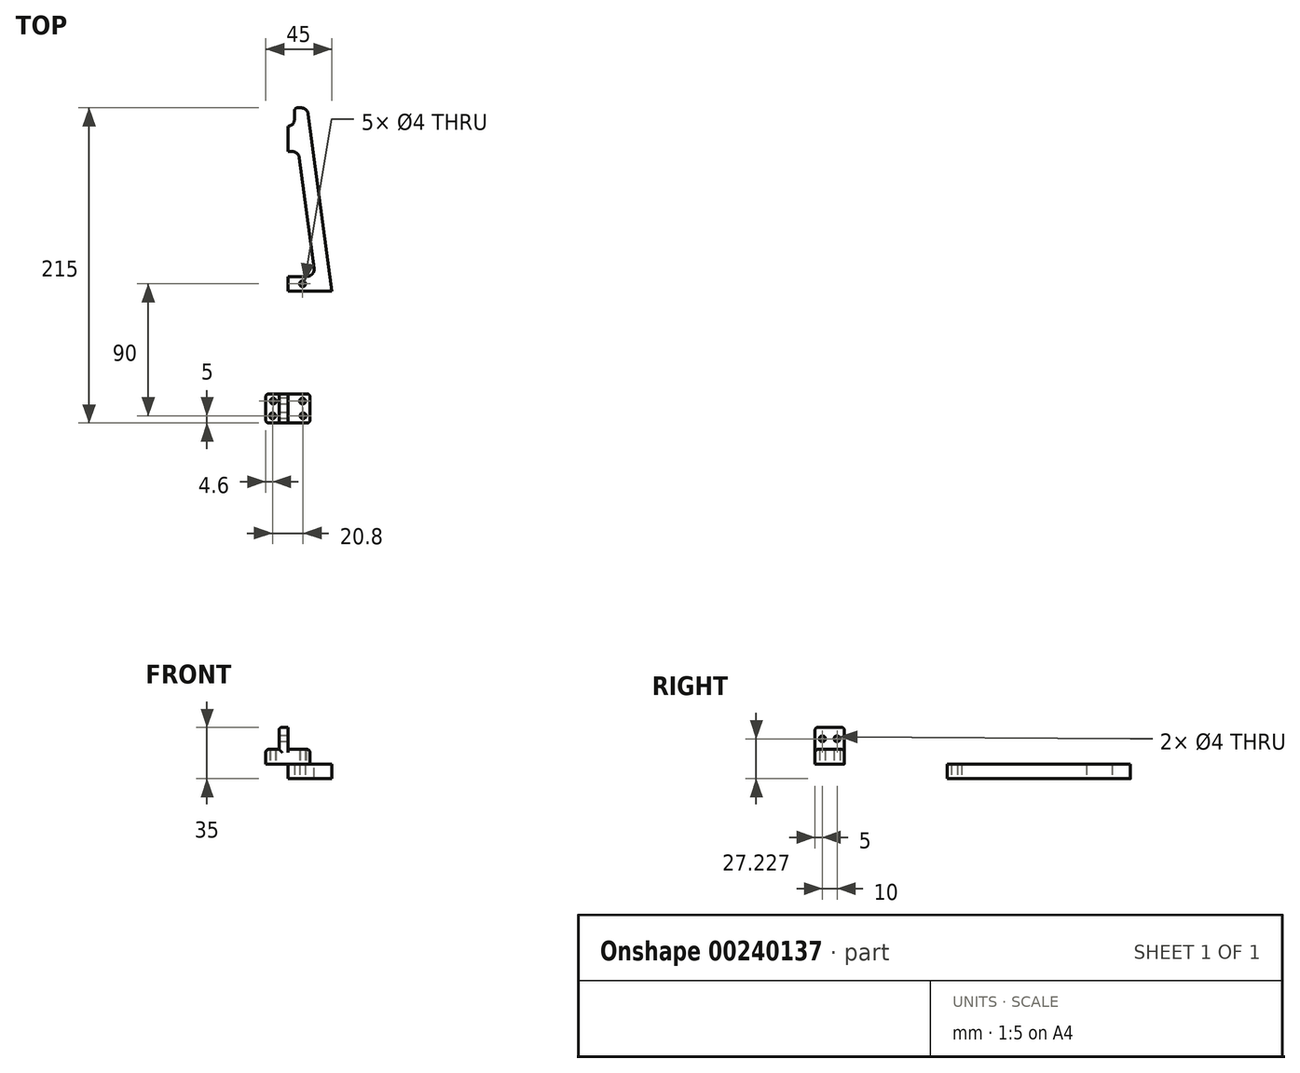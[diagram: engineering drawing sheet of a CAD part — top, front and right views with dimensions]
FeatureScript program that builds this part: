
annotation { "Feature Type Name" : "Feature", "Feature Type Description" : "" }
export const myFeature = defineFeature(function(context is Context, id is Id, definition is map)
    precondition{}
    {
        {
            var Q0;
            Q0=qCreatedBy(makeId("Top.planeOp"),FACE);
            var sketch = newSketch(context, id + "F0", { "sketchPlane" : qUnion([Q0])});
            skLineSegment(sketch, "E0.top", {"start": v(0, 75) * mm, "end": v(-30, 75) * mm});
            skPoint(sketch, "E0.middle", {"position": v(0, 0) * mm});
            skLineSegment(sketch, "E1", {"start": v(-30, 75) * mm, "end": v(-50, -75) * mm});
            skPoint(sketch, "E0.right.end.orphan", {"position": v(-50, 75) * mm});
            skPoint(sketch, "E0.left.end.orphan", {"position": v(50, 75) * mm});
            skLineSegment(sketch, "E2", {"start": v(0, 0) * mm, "end": v(0, 6) * mm});
            skLineSegment(sketch, "E3", {"start": v(-50, -75) * mm, "end": v(-40, -75) * mm});
            skLineSegment(sketch, "E4", {"start": v(-30, 75) * mm, "end": v(-20, 75) * mm});
            skLineSegment(sketch, "E5", {"start": v(0, 75) * mm, "end": v(0, 65) * mm});
            skLineSegment(sketch, "E6", {"start": v(0, 65) * mm, "end": v(-21.33, 65) * mm});
            skLineSegment(sketch, "E7", {"start": v(0, -75) * mm, "end": v(0, -65) * mm});
            skLineSegment(sketch, "E8", {"start": v(0, -65) * mm, "end": v(-38.67, -65) * mm});
            skLineSegment(sketch, "E9", {"start": v(0, 6) * mm, "end": v(-29.2, 6) * mm});
            skLineSegment(sketch, "E10", {"start": v(0, 0) * mm, "end": v(0, -6) * mm});
            skLineSegment(sketch, "E11", {"start": v(0, -6) * mm, "end": v(-30.8, -6) * mm});
            skLineSegment(sketch, "E12.trimOffspring", {"start": v(-30.8, -6) * mm, "end": v(-38.67, -65) * mm});
            skLineSegment(sketch, "E13", {"start": v(-21.33, 65) * mm, "end": v(-29.2, 6) * mm});
            skLineSegment(sketch, "E14.trimOffspring", {"start": v(0, -75) * mm, "end": v(-50, -75) * mm});
            skPoint(sketch, "E0.bottom.start.orphan", {"position": v(50, -75) * mm});
            skCircle(sketch, "E15", {"center": v(-15, 0) * mm, "radius": 2 * mm});
            skLineSegment(sketch, "E16", {"start": v(0, 65) * mm, "end": v(0, 70) * mm});
            skCircle(sketch, "E17", {"center": v(-10.41, 70) * mm, "radius": 2 * mm});
            skSolve(sketch);
        }
        {
            var Q0;
            Q0=qSketchRegion(id+"F0",true);
            extrude(context, id + "F1", {"entities" : qUnion([Q0]), "depth" : 10 * mm});
        }
        {
            var Q0;
            Q0=makeQuery(id+"F1.opExtrude","SWEPT_EDGE",EDGE,{"disambiguationData":[OSD([sQuery(id+"F0.wireOp",EDGE,"E6"),sQuery(id+"F0.wireOp",EDGE,"E13")])]});
            var Q1;
            Q1=makeQuery(id+"F1.opExtrude","SWEPT_EDGE",EDGE,{"disambiguationData":[OSD([sQuery(id+"F0.wireOp",EDGE,"E11"),sQuery(id+"F0.wireOp",EDGE,"E12.trimOffspring")])]});
            var Q2;
            Q2=makeQuery(id+"F1.opExtrude","SWEPT_EDGE",EDGE,{"disambiguationData":[OSD([sQuery(id+"F0.wireOp",EDGE,"E9"),sQuery(id+"F0.wireOp",EDGE,"E13")])]});
            var Q3;
            Q3=makeQuery(id+"F1.opExtrude","SWEPT_EDGE",EDGE,{"disambiguationData":[OSD([sQuery(id+"F0.wireOp",EDGE,"E8"),sQuery(id+"F0.wireOp",EDGE,"E12.trimOffspring")])]});
            var Q4;
            Q4=makeQuery(id+"F1.opExtrude","SWEPT_EDGE",EDGE,{"disambiguationData":[OSD([sQuery(id+"F0.wireOp",EDGE,"E1"),sQuery(id+"F0.wireOp",EDGE,"E14.trimOffspring")])]});
            fillet(context, id + "F2", {"entities" : qUnion([Q0, Q1, Q2, Q3, Q4]), "radius" : 5 * mm, "tangentPropagation" : true, "allowEdgeOverflow" : false});
        }
        {
            var Q0;
            Q0=makeQuery(id+"F1.opExtrude","SWEPT_BODY",BODY,{"disambiguationData":[OSD([sQuery(id+"F0.wireOp",EDGE,"E0.top"),sQuery(id+"F0.wireOp",EDGE,"E1"),sQuery(id+"F0.wireOp",EDGE,"E2"),sQuery(id+"F0.wireOp",EDGE,"E4"),sQuery(id+"F0.wireOp",EDGE,"E5"),sQuery(id+"F0.wireOp",EDGE,"E6"),sQuery(id+"F0.wireOp",EDGE,"E7"),sQuery(id+"F0.wireOp",EDGE,"E8"),sQuery(id+"F0.wireOp",EDGE,"E9"),sQuery(id+"F0.wireOp",EDGE,"E10"),sQuery(id+"F0.wireOp",EDGE,"E11"),sQuery(id+"F0.wireOp",EDGE,"E12.trimOffspring"),sQuery(id+"F0.wireOp",EDGE,"E13"),sQuery(id+"F0.wireOp",EDGE,"E14.trimOffspring"),sQuery(id+"F0.wireOp",EDGE,"E15"),sQuery(id+"F0.wireOp",EDGE,"E16"),sQuery(id+"F0.wireOp",EDGE,"E17")])]});
            var Q1;
            Q1=qCreatedBy(makeId("Right.planeOp"),FACE);
            mirror(context, id + "F3", {"operationType" : NewBodyOperationType.ADD, "entities" : qUnion([Q0]), "mirrorPlane" : qUnion([Q1])});
        }
        {
            var Q0;
            Q0=qCreatedBy(makeId("Top.planeOp"),FACE);
            var sketch = newSketch(context, id + "F4", { "sketchPlane" : qUnion([Q0])});
            skLineSegment(sketch, "E18", {"start": v(0, 0) * mm, "end": v(40, 0) * mm});
            skLineSegment(sketch, "E19", {"start": v(0, 75) * mm, "end": v(30, 75) * mm});
            skLineSegment(sketch, "E20", {"start": v(0, 75) * mm, "end": v(0, 85) * mm});
            skLineSegment(sketch, "E21", {"start": v(4.5, 200) * mm, "end": v(13.33, 200) * mm});
            skLineSegment(sketch, "E22", {"start": v(30, 75) * mm, "end": v(13.33, 200) * mm});
            skArc(sketch, "E23", {"start": v(0, 187.5) * mm, "mid": v(3.18, 188.82) * mm, "end": v(4.5, 192) * mm});
            skLineSegment(sketch, "E24", {"start": v(4.5, 200) * mm, "end": v(4.5, 192) * mm});
            skLineSegment(sketch, "E25", {"start": v(0, 75) * mm, "end": v(0, 80) * mm});
            skCircle(sketch, "E26", {"center": v(10, 80) * mm, "radius": 2 * mm});
            skLineSegment(sketch, "E27", {"start": v(0, 75) * mm, "end": v(10, 75) * mm});
            skLineSegment(sketch, "E28", {"start": v(10, 85) * mm, "end": v(18.67, 85) * mm});
            skLineSegment(sketch, "E29", {"start": v(18.67, 85) * mm, "end": v(10, 150) * mm});
            skLineSegment(sketch, "E30", {"start": v(10, 85) * mm, "end": v(0, 85) * mm});
            skLineSegment(sketch, "E31", {"start": v(18.67, 85) * mm, "end": v(7.31, 170.17) * mm});
            skLineSegment(sketch, "E32", {"start": v(7.31, 170.17) * mm, "end": v(0, 170.17) * mm});
            skLineSegment(sketch, "E33.trimOffspring", {"start": v(0, 170.17) * mm, "end": v(0, 187.5) * mm});
            skSolve(sketch);
        }
        {
            var Q0;
            Q0=qSketchRegion(id+"F4",true);
            extrude(context, id + "F5", {"entities" : qUnion([Q0]), "depth" : 10 * mm});
        }
        {
            var Q0;
            Q0=makeQuery(id+"F5.opExtrude","SWEPT_BODY",BODY,{"disambiguationData":[OSD([sQuery(id+"F4.wireOp",EDGE,"E19"),sQuery(id+"F4.wireOp",EDGE,"E20"),sQuery(id+"F4.wireOp",EDGE,"E21"),sQuery(id+"F4.wireOp",EDGE,"E22"),sQuery(id+"F4.wireOp",EDGE,"E23"),sQuery(id+"F4.wireOp",EDGE,"E24"),sQuery(id+"F4.wireOp",EDGE,"E25"),sQuery(id+"F4.wireOp",EDGE,"E26"),sQuery(id+"F4.wireOp",EDGE,"E27"),sQuery(id+"F4.wireOp",EDGE,"E28"),sQuery(id+"F4.wireOp",EDGE,"E30"),sQuery(id+"F4.wireOp",EDGE,"E31"),sQuery(id+"F4.wireOp",EDGE,"E32"),sQuery(id+"F4.wireOp",EDGE,"E33.trimOffspring")])]});
            var Q1;
            Q1=qCreatedBy(makeId("Right.planeOp"),FACE);
            mirror(context, id + "F6", {"entities" : qUnion([Q0]), "mirrorPlane" : qUnion([Q1])});
        }
        {
            var Q0;
            Q0=makeQuery(id+"F6.opPattern","COPY",EDGE,{"derivedFrom":makeQuery(id+"F5.opExtrude","SWEPT_EDGE",EDGE,{"disambiguationData":[OSD([sQuery(id+"F4.wireOp",EDGE,"E31"),sQuery(id+"F4.wireOp",EDGE,"E32")])]}),"instanceName":"1"});
            var Q1;
            Q1=makeQuery(id+"F5.opExtrude","SWEPT_EDGE",EDGE,{"disambiguationData":[OSD([sQuery(id+"F4.wireOp",EDGE,"E31"),sQuery(id+"F4.wireOp",EDGE,"E32")])]});
            var Q2;
            Q2=makeQuery(id+"F6.opPattern","COPY",EDGE,{"derivedFrom":makeQuery(id+"F5.opExtrude","SWEPT_EDGE",EDGE,{"disambiguationData":[OSD([sQuery(id+"F4.wireOp",EDGE,"E28"),sQuery(id+"F4.wireOp",EDGE,"E31")])]}),"instanceName":"1"});
            var Q3;
            Q3=makeQuery(id+"F5.opExtrude","SWEPT_EDGE",EDGE,{"disambiguationData":[OSD([sQuery(id+"F4.wireOp",EDGE,"E28"),sQuery(id+"F4.wireOp",EDGE,"E31")])]});
            var Q4;
            Q4=makeQuery(id+"F6.opPattern","COPY",EDGE,{"derivedFrom":makeQuery(id+"F5.opExtrude","SWEPT_EDGE",EDGE,{"disambiguationData":[OSD([sQuery(id+"F4.wireOp",EDGE,"E21"),sQuery(id+"F4.wireOp",EDGE,"E22")])]}),"instanceName":"1"});
            var Q5;
            Q5=makeQuery(id+"F5.opExtrude","SWEPT_EDGE",EDGE,{"disambiguationData":[OSD([sQuery(id+"F4.wireOp",EDGE,"E21"),sQuery(id+"F4.wireOp",EDGE,"E22")])]});
            fillet(context, id + "F7", {"entities" : qUnion([Q0, Q1, Q2, Q3, Q4, Q5]), "radius" : 5 * mm, "tangentPropagation" : true, "allowEdgeOverflow" : false});
        }
        {
            var Q0;
            Q0=makeQuery(id+"F5.opExtrude","SWEPT_EDGE",EDGE,{"disambiguationData":[OSD([sQuery(id+"F4.wireOp",EDGE,"E21"),sQuery(id+"F4.wireOp",EDGE,"E24")])]});
            var Q1;
            Q1=makeQuery(id+"F6.opPattern","COPY",EDGE,{"derivedFrom":makeQuery(id+"F5.opExtrude","SWEPT_EDGE",EDGE,{"disambiguationData":[OSD([sQuery(id+"F4.wireOp",EDGE,"E21"),sQuery(id+"F4.wireOp",EDGE,"E24")])]}),"instanceName":"1"});
            fillet(context, id + "F8", {"entities" : qUnion([Q0, Q1]), "radius" : 2 * mm, "tangentPropagation" : true, "allowEdgeOverflow" : false});
        }
        {
            var Q0;
            Q0=qCreatedBy(makeId("Top.planeOp"),FACE);
            var sketch = newSketch(context, id + "F9", { "sketchPlane" : qUnion([Q0])});
            skLineSegment(sketch, "E34", {"start": v(0, 0) * mm, "end": v(0, 6) * mm});
            skLineSegment(sketch, "E35", {"start": v(0, 6) * mm, "end": v(-6, 6) * mm});
            skLineSegment(sketch, "E36", {"start": v(-6, 6) * mm, "end": v(-6, -6) * mm});
            skLineSegment(sketch, "E37", {"start": v(-6, -6) * mm, "end": v(0, -6) * mm});
            skLineSegment(sketch, "E38", {"start": v(0, -6) * mm, "end": v(0, 0) * mm});
            skSolve(sketch);
        }
        {
            var Q0;
            Q0=qSketchRegion(id+"F9",true);
            extrude(context, id + "F10", {"entities" : qUnion([Q0]), "operationType" : NewBodyOperationType.ADD, "depth" : 25 * mm});
        }
        {
            var Q0;
            Q0=makeQuery(id+"F10.opExtrude","SWEPT_EDGE",EDGE,{"disambiguationData":[OSD([sQuery(id+"F9.wireOp",EDGE,"E36"),sQuery(id+"F9.wireOp",EDGE,"E37")])]});
            var Q1;
            Q1=makeQuery(id+"F10.opExtrude","CAP_EDGE",EDGE,{"disambiguationData":[OSD([sQuery(id+"F9.wireOp",EDGE,"E36")])],"isStart":false});
            var Q2;
            Q2=makeQuery(id+"F10.opExtrude","CAP_EDGE",EDGE,{"disambiguationData":[OSD([sQuery(id+"F9.wireOp",EDGE,"E37")])],"isStart":false});
            var Q3;
            Q3=makeQuery(id+"F10.opExtrude","SWEPT_EDGE",EDGE,{"disambiguationData":[OSD([sQuery(id+"F9.wireOp",EDGE,"E35"),sQuery(id+"F9.wireOp",EDGE,"E36")])]});
            var Q4;
            Q4=makeQuery(id+"F10.opExtrude","CAP_EDGE",EDGE,{"disambiguationData":[OSD([sQuery(id+"F9.wireOp",EDGE,"E35")])],"isStart":false});
            fillet(context, id + "F11", {"entities" : qUnion([Q0, Q1, Q2, Q3, Q4]), "radius" : 1.5 * mm, "tangentPropagation" : true, "allowEdgeOverflow" : false});
        }
        {
            var Q0;
            Q0=qCreatedBy(makeId("Right.planeOp"),FACE);
            var sketch = newSketch(context, id + "F12", { "sketchPlane" : qUnion([Q0])});
            skCircle(sketch, "E39", {"center": v(0, 20) * mm, "radius": 1.75 * mm});
            skCircle(sketch, "E40", {"center": v(0, 15) * mm, "radius": 1.75 * mm});
            skSolve(sketch);
        }
        {
            var Q0;
            Q0=qSketchRegion(id+"F12",true);
            extrude(context, id + "F13", {"entities" : qUnion([Q0]), "endBound" : BoundingType.SYMMETRIC, "depth" : 25 * mm});
        }
        {
            var Q0;
            Q0=makeQuery(id+"F13.opExtrude","SWEPT_BODY",BODY,{"disambiguationData":[OSD([sQuery(id+"F12.wireOp",EDGE,"E40")])]});
            var Q1;
            Q1=makeQuery(id+"F13.opExtrude","SWEPT_BODY",BODY,{"disambiguationData":[OSD([sQuery(id+"F12.wireOp",EDGE,"E39")])]});
            var Q2;
            Q2=makeQuery(id+"F1.opExtrude","SWEPT_BODY",BODY,{"disambiguationData":[OSD([sQuery(id+"F0.wireOp",EDGE,"E0.top"),sQuery(id+"F0.wireOp",EDGE,"E1"),sQuery(id+"F0.wireOp",EDGE,"E2"),sQuery(id+"F0.wireOp",EDGE,"E4"),sQuery(id+"F0.wireOp",EDGE,"E5"),sQuery(id+"F0.wireOp",EDGE,"E6"),sQuery(id+"F0.wireOp",EDGE,"E7"),sQuery(id+"F0.wireOp",EDGE,"E8"),sQuery(id+"F0.wireOp",EDGE,"E9"),sQuery(id+"F0.wireOp",EDGE,"E10"),sQuery(id+"F0.wireOp",EDGE,"E11"),sQuery(id+"F0.wireOp",EDGE,"E12.trimOffspring"),sQuery(id+"F0.wireOp",EDGE,"E13"),sQuery(id+"F0.wireOp",EDGE,"E14.trimOffspring"),sQuery(id+"F0.wireOp",EDGE,"E15"),sQuery(id+"F0.wireOp",EDGE,"E16"),sQuery(id+"F0.wireOp",EDGE,"E17")])]});
            booleanBodies(context, id + "F14", {"operationType" : BooleanOperationType.SUBTRACTION, "tools" : qUnion([Q0, Q1]), "targets" : qUnion([Q2])});
        }
        {
            var Q0;
            Q0=qCreatedBy(makeId("Top.planeOp"),FACE);
            var sketch = newSketch(context, id + "F15", { "sketchPlane" : qUnion([Q0])});
            skLineSegment(sketch, "E41.bottom", {"start": v(15, 65) * mm, "end": v(-15, 65) * mm});
            skLineSegment(sketch, "E41.top", {"start": v(15, 85) * mm, "end": v(-15, 85) * mm});
            skLineSegment(sketch, "E41.left", {"start": v(15, 65) * mm, "end": v(15, 85) * mm});
            skLineSegment(sketch, "E41.right", {"start": v(-15, 65) * mm, "end": v(-15, 85) * mm});
            skPoint(sketch, "E41.middle", {"position": v(0, 75) * mm});
            skLineSegment(sketch, "E42", {"start": v(0, 75) * mm, "end": v(0, 85) * mm});
            skLineSegment(sketch, "E43", {"start": v(0, 85) * mm, "end": v(0, 65) * mm});
            skLineSegment(sketch, "E44", {"start": v(0, 65) * mm, "end": v(-6, 65) * mm});
            skLineSegment(sketch, "E45", {"start": v(-6, 65) * mm, "end": v(-6, 85) * mm});
            skLineSegment(sketch, "E46", {"start": v(-6, 85) * mm, "end": v(0, 85) * mm});
            skSolve(sketch);
        }
        {
            var Q0;
            Q0=qSketchRegion(id+"F15",true);
            extrude(context, id + "F16", {"entities" : qUnion([Q0]), "depth" : 10 * mm});
        }
        {
            var Q0;
            Q0=qCreatedBy(makeId("Top.planeOp"),FACE);
            var sketch = newSketch(context, id + "F17", { "sketchPlane" : qUnion([Q0])});
            skLineSegment(sketch, "E47", {"start": v(0, 65) * mm, "end": v(0, 85) * mm});
            skLineSegment(sketch, "E48", {"start": v(0, 85) * mm, "end": v(-6, 85) * mm});
            skLineSegment(sketch, "E49", {"start": v(-6, 85) * mm, "end": v(-6, 65) * mm});
            skLineSegment(sketch, "E50", {"start": v(-6, 65) * mm, "end": v(0, 65) * mm});
            skSolve(sketch);
        }
        {
            var Q0;
            Q0=qSketchRegion(id+"F17",true);
            extrude(context, id + "F18", {"entities" : qUnion([Q0]), "depth" : 25 * mm});
        }
        {
            var Q0;
            Q0=makeQuery(id+"F16.opExtrude","SWEPT_BODY",BODY,{"disambiguationData":[OSD([sQuery(id+"F15.wireOp",EDGE,"E41.bottom"),sQuery(id+"F15.wireOp",EDGE,"E41.top"),sQuery(id+"F15.wireOp",EDGE,"E41.left"),sQuery(id+"F15.wireOp",EDGE,"E41.right"),sQuery(id+"F15.wireOp",EDGE,"E44"),sQuery(id+"F15.wireOp",EDGE,"E46")])]});
            var Q1;
            Q1=makeQuery(id+"F18.opExtrude","SWEPT_BODY",BODY,{"disambiguationData":[OSD([sQuery(id+"F17.wireOp",EDGE,"E47"),sQuery(id+"F17.wireOp",EDGE,"E48"),sQuery(id+"F17.wireOp",EDGE,"E49"),sQuery(id+"F17.wireOp",EDGE,"E50")])]});
            booleanBodies(context, id + "F19", {"operationType" : BooleanOperationType.UNION, "tools" : qUnion([Q0, Q1])});
        }
        {
            var Q0;
            Q0=makeQuery(id+"F16.opExtrude","SWEPT_BODY",BODY,{"disambiguationData":[OSD([sQuery(id+"F15.wireOp",EDGE,"E41.bottom"),sQuery(id+"F15.wireOp",EDGE,"E41.top"),sQuery(id+"F15.wireOp",EDGE,"E41.left"),sQuery(id+"F15.wireOp",EDGE,"E41.right"),sQuery(id+"F15.wireOp",EDGE,"E44"),sQuery(id+"F15.wireOp",EDGE,"E46")])]});
            transform(context, id + "F20", {"entities" : qUnion([Q0]), "transformType" : TransformType.TRANSLATION_3D, "dx" : 0 * mm, "dy" : 0 * mm, "dz" : 10 * mm, "makeCopy" : false});
        }
        {
            var Q0;
            Q0=qCreatedBy(makeId("Top.planeOp"),FACE);
            var sketch = newSketch(context, id + "F21", { "sketchPlane" : qUnion([Q0])});
            skCircle(sketch, "E51", {"center": v(-10, 80) * mm, "radius": 2 * mm});
            skCircle(sketch, "E52", {"center": v(10, 80) * mm, "radius": 2 * mm});
            skCircle(sketch, "E53", {"center": v(-10.4, 70) * mm, "radius": 2 * mm});
            skCircle(sketch, "E54", {"center": v(10.4, 70) * mm, "radius": 2 * mm});
            skSolve(sketch);
        }
        {
            var Q0;
            Q0=qSketchRegion(id+"F21",true);
            extrude(context, id + "F22", {"entities" : qUnion([Q0]), "depth" : 30 * mm});
        }
        {
            var Q0;
            Q0=makeQuery(id+"F22.opExtrude","SWEPT_BODY",BODY,{"disambiguationData":[OSD([sQuery(id+"F21.wireOp",EDGE,"E54")])]});
            var Q1;
            Q1=makeQuery(id+"F22.opExtrude","SWEPT_BODY",BODY,{"disambiguationData":[OSD([sQuery(id+"F21.wireOp",EDGE,"E53")])]});
            var Q2;
            Q2=makeQuery(id+"F22.opExtrude","SWEPT_BODY",BODY,{"disambiguationData":[OSD([sQuery(id+"F21.wireOp",EDGE,"E52")])]});
            var Q3;
            Q3=makeQuery(id+"F22.opExtrude","SWEPT_BODY",BODY,{"disambiguationData":[OSD([sQuery(id+"F21.wireOp",EDGE,"E51")])]});
            var Q4;
            Q4=makeQuery(id+"F16.opExtrude","SWEPT_BODY",BODY,{"disambiguationData":[OSD([sQuery(id+"F15.wireOp",EDGE,"E41.bottom"),sQuery(id+"F15.wireOp",EDGE,"E41.top"),sQuery(id+"F15.wireOp",EDGE,"E41.left"),sQuery(id+"F15.wireOp",EDGE,"E41.right"),sQuery(id+"F15.wireOp",EDGE,"E44"),sQuery(id+"F15.wireOp",EDGE,"E46")])]});
            booleanBodies(context, id + "F23", {"operationType" : BooleanOperationType.SUBTRACTION, "tools" : qUnion([Q0, Q1, Q2, Q3]), "targets" : qUnion([Q4])});
        }
        {
            var Q0;
            Q0=qCreatedBy(makeId("Right.planeOp"),FACE);
            var sketch = newSketch(context, id + "F24", { "sketchPlane" : qUnion([Q0])});
            skCircle(sketch, "E55", {"center": v(80, 27.23) * mm, "radius": 2 * mm});
            skCircle(sketch, "E56", {"center": v(70, 27.23) * mm, "radius": 2 * mm});
            skSolve(sketch);
        }
        {
            var Q0;
            Q0=qSketchRegion(id+"F24",true);
            extrude(context, id + "F25", {"entities" : qUnion([Q0]), "endBound" : BoundingType.SYMMETRIC, "depth" : 25 * mm});
        }
        {
            var Q0;
            Q0=makeQuery(id+"F25.opExtrude","SWEPT_BODY",BODY,{"disambiguationData":[OSD([sQuery(id+"F24.wireOp",EDGE,"E56")])]});
            var Q1;
            Q1=makeQuery(id+"F25.opExtrude","SWEPT_BODY",BODY,{"disambiguationData":[OSD([sQuery(id+"F24.wireOp",EDGE,"E55")])]});
            var Q2;
            Q2=makeQuery(id+"F16.opExtrude","SWEPT_BODY",BODY,{"disambiguationData":[OSD([sQuery(id+"F15.wireOp",EDGE,"E41.bottom"),sQuery(id+"F15.wireOp",EDGE,"E41.top"),sQuery(id+"F15.wireOp",EDGE,"E41.left"),sQuery(id+"F15.wireOp",EDGE,"E41.right"),sQuery(id+"F15.wireOp",EDGE,"E44"),sQuery(id+"F15.wireOp",EDGE,"E46")])]});
            booleanBodies(context, id + "F26", {"operationType" : BooleanOperationType.SUBTRACTION, "tools" : qUnion([Q0, Q1]), "targets" : qUnion([Q2])});
        }
        {
            var Q0;
            Q0=makeQuery(id+"F18.opExtrude","SWEPT_EDGE",EDGE,{"disambiguationData":[OSD([sQuery(id+"F17.wireOp",EDGE,"E49"),sQuery(id+"F17.wireOp",EDGE,"E50")])]});
            var Q1;
            Q1=makeQuery(id+"F18.opExtrude","CAP_EDGE",EDGE,{"disambiguationData":[OSD([sQuery(id+"F17.wireOp",EDGE,"E50")])],"isStart":false});
            var Q2;
            {var subQ0=sQuery(id+"F15.wireOp",EDGE,"E44");var subQ1=sQuery(id+"F15.wireOp",EDGE,"E41.bottom");var subQ2=sQuery(id+"F15.wireOp",EDGE,"E41.right");Q2=makeQuery(id+"F19.opBoolean","SPLIT",EDGE,{"disambiguationData":[TD([makeQuery(id+"F16.opExtrude","SWEPT_FACE",FACE,{"disambiguationData":[OSD([subQ2])]})])],"derivedFrom":makeQuery(id+"F16.opExtrude","CAP_EDGE",EDGE,{"disambiguationData":[OSD([subQ1,subQ0])],"isStart":false})});}
            var Q3;
            Q3=makeQuery(id+"F16.opExtrude","SWEPT_EDGE",EDGE,{"disambiguationData":[OSD([sQuery(id+"F15.wireOp",EDGE,"E41.bottom"),sQuery(id+"F15.wireOp",EDGE,"E41.right")])]});
            var Q4;
            {var subQ0=sQuery(id+"F15.wireOp",EDGE,"E41.left");var subQ1=sQuery(id+"F15.wireOp",EDGE,"E44");var subQ2=sQuery(id+"F15.wireOp",EDGE,"E41.bottom");Q4=makeQuery(id+"F19.opBoolean","SPLIT",EDGE,{"disambiguationData":[TD([makeQuery(id+"F16.opExtrude","SWEPT_FACE",FACE,{"disambiguationData":[OSD([subQ0])]})])],"derivedFrom":makeQuery(id+"F16.opExtrude","CAP_EDGE",EDGE,{"disambiguationData":[OSD([subQ2,subQ1])],"isStart":false})});}
            var Q5;
            Q5=makeQuery(id+"F16.opExtrude","SWEPT_EDGE",EDGE,{"disambiguationData":[OSD([sQuery(id+"F15.wireOp",EDGE,"E41.bottom"),sQuery(id+"F15.wireOp",EDGE,"E41.left")])]});
            var Q6;
            Q6=makeQuery(id+"F16.opExtrude","CAP_EDGE",EDGE,{"disambiguationData":[OSD([sQuery(id+"F15.wireOp",EDGE,"E41.left")])],"isStart":false});
            var Q7;
            Q7=makeQuery(id+"F16.opExtrude","CAP_EDGE",EDGE,{"disambiguationData":[OSD([sQuery(id+"F15.wireOp",EDGE,"E41.right")])],"isStart":false});
            var Q8;
            Q8=makeQuery(id+"F18.opExtrude","CAP_EDGE",EDGE,{"disambiguationData":[OSD([sQuery(id+"F17.wireOp",EDGE,"E49")])],"isStart":false});
            var Q9;
            {var subQ0=sQuery(id+"F15.wireOp",EDGE,"E41.right");var subQ1=sQuery(id+"F15.wireOp",EDGE,"E46");var subQ2=sQuery(id+"F15.wireOp",EDGE,"E41.top");Q9=makeQuery(id+"F19.opBoolean","SPLIT",EDGE,{"disambiguationData":[TD([makeQuery(id+"F16.opExtrude","SWEPT_FACE",FACE,{"disambiguationData":[OSD([subQ0])]})])],"derivedFrom":makeQuery(id+"F16.opExtrude","CAP_EDGE",EDGE,{"disambiguationData":[OSD([subQ2,subQ1])],"isStart":false})});}
            var Q10;
            Q10=makeQuery(id+"F16.opExtrude","SWEPT_EDGE",EDGE,{"disambiguationData":[OSD([sQuery(id+"F15.wireOp",EDGE,"E41.top"),sQuery(id+"F15.wireOp",EDGE,"E41.right")])]});
            var Q11;
            Q11=makeQuery(id+"F18.opExtrude","SWEPT_EDGE",EDGE,{"disambiguationData":[OSD([sQuery(id+"F17.wireOp",EDGE,"E48"),sQuery(id+"F17.wireOp",EDGE,"E49")])]});
            var Q12;
            Q12=makeQuery(id+"F18.opExtrude","CAP_EDGE",EDGE,{"disambiguationData":[OSD([sQuery(id+"F17.wireOp",EDGE,"E48")])],"isStart":false});
            var Q13;
            {var subQ0=sQuery(id+"F15.wireOp",EDGE,"E41.left");var subQ1=sQuery(id+"F15.wireOp",EDGE,"E46");var subQ2=sQuery(id+"F15.wireOp",EDGE,"E41.top");Q13=makeQuery(id+"F19.opBoolean","SPLIT",EDGE,{"disambiguationData":[TD([makeQuery(id+"F16.opExtrude","SWEPT_FACE",FACE,{"disambiguationData":[OSD([subQ0])]})])],"derivedFrom":makeQuery(id+"F16.opExtrude","CAP_EDGE",EDGE,{"disambiguationData":[OSD([subQ2,subQ1])],"isStart":false})});}
            var Q14;
            Q14=makeQuery(id+"F16.opExtrude","SWEPT_EDGE",EDGE,{"disambiguationData":[OSD([sQuery(id+"F15.wireOp",EDGE,"E41.top"),sQuery(id+"F15.wireOp",EDGE,"E41.left")])]});
            fillet(context, id + "F27", {"entities" : qUnion([Q0, Q1, Q2, Q3, Q4, Q5, Q6, Q7, Q8, Q9, Q10, Q11, Q12, Q13, Q14]), "radius" : 2 * mm, "tangentPropagation" : true, "allowEdgeOverflow" : false});
        }
        {
            var Q0;
            Q0=qCreatedBy(makeId("Right.planeOp"),FACE);
            var sketch = newSketch(context, id + "F28", { "sketchPlane" : qUnion([Q0])});
            skLineSegment(sketch, "E57", {"start": v(0, 0) * mm, "end": v(0, 10) * mm});
            skLineSegment(sketch, "E58", {"start": v(0, 10) * mm, "end": v(6, 10) * mm});
            skLineSegment(sketch, "E59", {"start": v(6, 10) * mm, "end": v(6, 25) * mm});
            skLineSegment(sketch, "E60", {"start": v(-6, 25) * mm, "end": v(-6, 10) * mm});
            skLineSegment(sketch, "E61", {"start": v(-6, 10) * mm, "end": v(0, 10) * mm});
            skLineSegment(sketch, "E62", {"start": v(75, 10) * mm, "end": v(75, 20) * mm});
            skLineSegment(sketch, "E63", {"start": v(75, 20) * mm, "end": v(85, 20) * mm});
            skLineSegment(sketch, "E64", {"start": v(85, 20) * mm, "end": v(85, 35) * mm});
            skLineSegment(sketch, "E65", {"start": v(65, 35) * mm, "end": v(65, 20) * mm});
            skLineSegment(sketch, "E66", {"start": v(65, 20) * mm, "end": v(75, 20) * mm});
            skLineSegment(sketch, "E67", {"start": v(-6, 10) * mm, "end": v(-6, 25) * mm});
            skLineSegment(sketch, "E68", {"start": v(75, 120) * mm, "end": v(85, 120) * mm});
            skLineSegment(sketch, "E69", {"start": v(85, 35) * mm, "end": v(85, 120) * mm});
            skLineSegment(sketch, "E70", {"start": v(85, 120) * mm, "end": v(75, 120) * mm});
            skLineSegment(sketch, "E71", {"start": v(6, 25) * mm, "end": v(65, 35) * mm});
            skLineSegment(sketch, "E72", {"start": v(-6, 25) * mm, "end": v(75, 120) * mm});
            skLineSegment(sketch, "E73", {"start": v(23.92, 44.68) * mm, "end": v(75, 104.59) * mm});
            skLineSegment(sketch, "E74", {"start": v(23.92, 44.68) * mm, "end": v(17.44, 37.08) * mm});
            skLineSegment(sketch, "E75", {"start": v(75, 45) * mm, "end": v(64.16, 45) * mm});
            skLineSegment(sketch, "E76", {"start": v(51.92, 42.93) * mm, "end": v(17.44, 37.08) * mm});
            skLineSegment(sketch, "E77", {"start": v(51.92, 42.93) * mm, "end": v(64.16, 45) * mm});
            skPoint(sketch, "E78.orphan", {"position": v(75, 35) * mm});
            skPoint(sketch, "E79.start.orphan", {"position": v(75, 110) * mm});
            skLineSegment(sketch, "E80", {"start": v(75, 104.59) * mm, "end": v(75, 45) * mm});
            skCircle(sketch, "E81", {"center": v(80, 110) * mm, "radius": 2 * mm});
            skCircle(sketch, "E82", {"center": v(80, 95) * mm, "radius": 2 * mm});
            skPoint(sketch, "E83.end.orphan", {"position": v(80, 120) * mm});
            skSolve(sketch);
        }
        {
            var Q0;
            Q0=qSketchRegion(id+"F28",true);
            extrude(context, id + "F29", {"entities" : qUnion([Q0]), "depth" : 8 * mm});
        }
        {
            var Q0;
            Q0=makeQuery(id+"F29.opExtrude","SWEPT_EDGE",EDGE,{"disambiguationData":[OSD([sQuery(id+"F28.wireOp",EDGE,"E73"),sQuery(id+"F28.wireOp",EDGE,"E80")])]});
            var Q1;
            Q1=makeQuery(id+"F29.opExtrude","SWEPT_EDGE",EDGE,{"disambiguationData":[OSD([sQuery(id+"F28.wireOp",EDGE,"E75"),sQuery(id+"F28.wireOp",EDGE,"E80")])]});
            var Q2;
            Q2=makeQuery(id+"F29.opExtrude","SWEPT_EDGE",EDGE,{"disambiguationData":[OSD([sQuery(id+"F28.wireOp",EDGE,"E74"),sQuery(id+"F28.wireOp",EDGE,"E76")])]});
            var Q3;
            Q3=makeQuery(id+"F29.opExtrude","SWEPT_EDGE",EDGE,{"disambiguationData":[OSD([sQuery(id+"F28.wireOp",EDGE,"E65"),sQuery(id+"F28.wireOp",EDGE,"E71")])]});
            var Q4;
            Q4=makeQuery(id+"F29.opExtrude","SWEPT_EDGE",EDGE,{"disambiguationData":[OSD([sQuery(id+"F28.wireOp",EDGE,"E59"),sQuery(id+"F28.wireOp",EDGE,"E71")])]});
            var Q5;
            Q5=makeQuery(id+"F29.opExtrude","SWEPT_EDGE",EDGE,{"disambiguationData":[OSD([sQuery(id+"F28.wireOp",EDGE,"E67"),sQuery(id+"F28.wireOp",EDGE,"E72")])]});
            fillet(context, id + "F30", {"entities" : qUnion([Q0, Q1, Q2, Q3, Q4, Q5]), "radius" : 2 * mm, "tangentPropagation" : true, "allowEdgeOverflow" : false});
        }
        {
            var Q0;
            Q0=makeQuery(id+"F29.opExtrude","CAP_EDGE",EDGE,{"disambiguationData":[OSD([sQuery(id+"F28.wireOp",EDGE,"E73"),sQuery(id+"F28.wireOp",EDGE,"E74")])],"isStart":false});
            var Q1;
            Q1=makeQuery(id+"F29.opExtrude","CAP_EDGE",EDGE,{"disambiguationData":[OSD([sQuery(id+"F28.wireOp",EDGE,"E72")])],"isStart":false});
            var Q2;
            Q2=makeQuery(id+"F29.opExtrude","CAP_EDGE",EDGE,{"disambiguationData":[OSD([sQuery(id+"F28.wireOp",EDGE,"E71")])],"isStart":false});
            var Q3;
            Q3=makeQuery(id+"F29.opExtrude","CAP_EDGE",EDGE,{"disambiguationData":[OSD([sQuery(id+"F28.wireOp",EDGE,"E64"),sQuery(id+"F28.wireOp",EDGE,"E69")])],"isStart":false});
            fillet(context, id + "F31", {"entities" : qUnion([Q0, Q1, Q2, Q3]), "radius" : 2 * mm, "tangentPropagation" : true, "allowEdgeOverflow" : false});
        }
        {
            var Q0;
            Q0=qCreatedBy(makeId("Right.planeOp"),FACE);
            var sketch = newSketch(context, id + "F32", { "sketchPlane" : qUnion([Q0])});
            skCircle(sketch, "E84", {"center": v(0, 20) * mm, "radius": 1.75 * mm});
            skCircle(sketch, "E85", {"center": v(0, 15) * mm, "radius": 1.75 * mm});
            skCircle(sketch, "E86", {"center": v(70, 27.25) * mm, "radius": 2 * mm});
            skCircle(sketch, "E87", {"center": v(80, 27.25) * mm, "radius": 2 * mm});
            skSolve(sketch);
        }
        {
            var Q0;
            Q0=qSketchRegion(id+"F32",true);
            extrude(context, id + "F33", {"entities" : qUnion([Q0]), "depth" : 25 * mm});
        }
        {
            var Q0;
            Q0=makeQuery(id+"F33.opExtrude","SWEPT_BODY",BODY,{"disambiguationData":[OSD([sQuery(id+"F32.wireOp",EDGE,"E87")])]});
            var Q1;
            Q1=makeQuery(id+"F33.opExtrude","SWEPT_BODY",BODY,{"disambiguationData":[OSD([sQuery(id+"F32.wireOp",EDGE,"E86")])]});
            var Q2;
            Q2=makeQuery(id+"F33.opExtrude","SWEPT_BODY",BODY,{"disambiguationData":[OSD([sQuery(id+"F32.wireOp",EDGE,"E85")])]});
            var Q3;
            Q3=makeQuery(id+"F33.opExtrude","SWEPT_BODY",BODY,{"disambiguationData":[OSD([sQuery(id+"F32.wireOp",EDGE,"E84")])]});
            var Q4;
            Q4=makeQuery(id+"F29.opExtrude","SWEPT_BODY",BODY,{"disambiguationData":[OSD([sQuery(id+"F28.wireOp",EDGE,"E59"),sQuery(id+"F28.wireOp",EDGE,"E61"),sQuery(id+"F28.wireOp",EDGE,"E58"),sQuery(id+"F28.wireOp",EDGE,"E63"),sQuery(id+"F28.wireOp",EDGE,"E64"),sQuery(id+"F28.wireOp",EDGE,"E65"),sQuery(id+"F28.wireOp",EDGE,"E66"),sQuery(id+"F28.wireOp",EDGE,"E67"),sQuery(id+"F28.wireOp",EDGE,"E69"),sQuery(id+"F28.wireOp",EDGE,"E70"),sQuery(id+"F28.wireOp",EDGE,"E71"),sQuery(id+"F28.wireOp",EDGE,"E72"),sQuery(id+"F28.wireOp",EDGE,"E73"),sQuery(id+"F28.wireOp",EDGE,"E74"),sQuery(id+"F28.wireOp",EDGE,"E75"),sQuery(id+"F28.wireOp",EDGE,"E76"),sQuery(id+"F28.wireOp",EDGE,"E77"),sQuery(id+"F28.wireOp",EDGE,"E80"),sQuery(id+"F28.wireOp",EDGE,"E81"),sQuery(id+"F28.wireOp",EDGE,"E82")])]});
            booleanBodies(context, id + "F34", {"operationType" : BooleanOperationType.SUBTRACTION, "tools" : qUnion([Q0, Q1, Q2, Q3]), "targets" : qUnion([Q4])});
        }
        {
            var Q0;
            Q0=makeQuery(id+"F29.opExtrude","SWEPT_BODY",BODY,{"disambiguationData":[OSD([sQuery(id+"F28.wireOp",EDGE,"E59"),sQuery(id+"F28.wireOp",EDGE,"E61"),sQuery(id+"F28.wireOp",EDGE,"E58"),sQuery(id+"F28.wireOp",EDGE,"E63"),sQuery(id+"F28.wireOp",EDGE,"E64"),sQuery(id+"F28.wireOp",EDGE,"E65"),sQuery(id+"F28.wireOp",EDGE,"E66"),sQuery(id+"F28.wireOp",EDGE,"E67"),sQuery(id+"F28.wireOp",EDGE,"E69"),sQuery(id+"F28.wireOp",EDGE,"E70"),sQuery(id+"F28.wireOp",EDGE,"E71"),sQuery(id+"F28.wireOp",EDGE,"E72"),sQuery(id+"F28.wireOp",EDGE,"E73"),sQuery(id+"F28.wireOp",EDGE,"E74"),sQuery(id+"F28.wireOp",EDGE,"E75"),sQuery(id+"F28.wireOp",EDGE,"E76"),sQuery(id+"F28.wireOp",EDGE,"E77"),sQuery(id+"F28.wireOp",EDGE,"E80"),sQuery(id+"F28.wireOp",EDGE,"E81"),sQuery(id+"F28.wireOp",EDGE,"E82")])]});
            var Q1;
            Q1=makeQuery(id+"F6.opPattern","COPY",BODY,{"derivedFrom":makeQuery(id+"F5.opExtrude","SWEPT_BODY",BODY,{"disambiguationData":[OSD([sQuery(id+"F4.wireOp",EDGE,"E19"),sQuery(id+"F4.wireOp",EDGE,"E20"),sQuery(id+"F4.wireOp",EDGE,"E21"),sQuery(id+"F4.wireOp",EDGE,"E22"),sQuery(id+"F4.wireOp",EDGE,"E23"),sQuery(id+"F4.wireOp",EDGE,"E24"),sQuery(id+"F4.wireOp",EDGE,"E25"),sQuery(id+"F4.wireOp",EDGE,"E26"),sQuery(id+"F4.wireOp",EDGE,"E27"),sQuery(id+"F4.wireOp",EDGE,"E28"),sQuery(id+"F4.wireOp",EDGE,"E30"),sQuery(id+"F4.wireOp",EDGE,"E31"),sQuery(id+"F4.wireOp",EDGE,"E32"),sQuery(id+"F4.wireOp",EDGE,"E33.trimOffspring")])]}),"instanceName":"1"});
            var Q2;
            Q2=makeQuery(id+"F1.opExtrude","SWEPT_BODY",BODY,{"disambiguationData":[OSD([sQuery(id+"F0.wireOp",EDGE,"E0.top"),sQuery(id+"F0.wireOp",EDGE,"E1"),sQuery(id+"F0.wireOp",EDGE,"E2"),sQuery(id+"F0.wireOp",EDGE,"E4"),sQuery(id+"F0.wireOp",EDGE,"E5"),sQuery(id+"F0.wireOp",EDGE,"E6"),sQuery(id+"F0.wireOp",EDGE,"E7"),sQuery(id+"F0.wireOp",EDGE,"E8"),sQuery(id+"F0.wireOp",EDGE,"E9"),sQuery(id+"F0.wireOp",EDGE,"E10"),sQuery(id+"F0.wireOp",EDGE,"E11"),sQuery(id+"F0.wireOp",EDGE,"E12.trimOffspring"),sQuery(id+"F0.wireOp",EDGE,"E13"),sQuery(id+"F0.wireOp",EDGE,"E14.trimOffspring"),sQuery(id+"F0.wireOp",EDGE,"E15"),sQuery(id+"F0.wireOp",EDGE,"E16"),sQuery(id+"F0.wireOp",EDGE,"E17")])]});
            deleteBodies(context, id + "F35", {"entities" : qUnion([Q0, Q1, Q2])});
        }
        {
            var Q0;
            Q0=makeQuery(id+"F16.opExtrude","SWEPT_BODY",BODY,{"disambiguationData":[OSD([sQuery(id+"F15.wireOp",EDGE,"E41.bottom"),sQuery(id+"F15.wireOp",EDGE,"E41.top"),sQuery(id+"F15.wireOp",EDGE,"E41.left"),sQuery(id+"F15.wireOp",EDGE,"E41.right"),sQuery(id+"F15.wireOp",EDGE,"E44"),sQuery(id+"F15.wireOp",EDGE,"E46")])]});
            transform(context, id + "F36", {"entities" : qUnion([Q0]), "transformType" : TransformType.TRANSLATION_3D, "dx" : 0 * mm, "dy" : -80 * mm, "dz" : 0 * mm, "makeCopy" : false});
        }
    });
